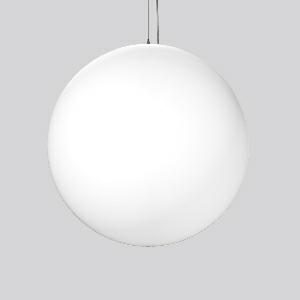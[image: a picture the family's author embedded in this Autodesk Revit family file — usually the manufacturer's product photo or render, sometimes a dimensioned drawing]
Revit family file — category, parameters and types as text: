
# Revit family: basic_ball_312108_002_76_694c
name_source: partatom
category: Lighting Fixtures
units: mm (PartAtom-declared; Revit-internal decimal feet)

## family parameters
Cut with Voids When Loaded = No
Host = Face
Light Source = No
Part Type = Normal
Room Calculation Point = No
Round Connector Dimension = Use Diameter
Shared = No

## types (1)
- BASIC BALL (1 x LED Modul 930, 8400 lm, 3000)
    Apparent Load = 79 VA
    CIE Flux Codes = 23 48 74 52 100
    Color Rendering = 90
    Color Temperature = 3000
    Default Elevation = 1800 mm
    Description = Series: BASIC BALL
Pendant luminaire in timelessly classic sphere design. Canopy: metal, powder-coated, white. Metal cap: white, powder-coated. Diffuser: mouth-blown opal glass, satin finish. Shadow-free, homogeneous and soft illumination. Single-point steel cable suspension, steplessly adjustable. Special lengths available on request. Power supply cable: white. 
Colour: white
Diameter: 600 mm
Height: 600 mm
Suspension length: 300-4000 mm
Lamp: LED
Socket: without socket
Colour temperature: 3000K
Colour rendering index (CRI): 90
System power: 79 W
Rated luminous flux: 8400 lm
Luminous efficiency: 106 lm/W
Control gear: Converter, dimmable, DALI
Protection class: I
Type of protection: IP 40
    Height = 600 mm
    Lamp = 1 x LED Modul 930
    Lamp Light Flux = 8400 lm
    Lamp count = 1
    Length = 600 mm
    Lifetime = 50000 h
    Luminous efficacy = 106 lm/W
    Manufacturer = RZB
    ModVariant = No
    Model = 312108.002.76
    Mounting Place = Ceiling
    Mounting Type = Pendant
    Number of Poles = 1
    OnlyDefault = Yes
    Power Factor = 1
    Product Name = BASIC BALL
    Product group = Pendant luminaires
    ProductGroupID = 902
    Protection Class = Protection class I
    Protection Degree = IP 40
    RLX_Detail_Level = 1
    RLX_Emergency_Light_Flux = 0 lm
    RLX_Emergency_Type = 0
    RLX_Emergency_Type_DB = No
    RlxData = <blob elided: 121265 chars, md5=2e508b57>
    Socket = socket
    Standby Power = 0 W
    System Light Flux = 8400 lm
    System Power = 79 W
    Type Comments = Product without accessories
    Type Image = 312108.002.jpg
    URL = http://relux.com
    VarID = ---
    Voltage = 230 V
    Voltage Range = 220-240 V
    Weight = 0.00 kg
    Width = 0 mm  [stored 0 ft]

note: [stored X ft] marks values corroborated as IEEE doubles in the binary element streams (Revit-internal decimal feet)

## geometry (parser evidence)
native form markers: Blend x4, Sweep x12
no freeform markers — native parametric forms only
